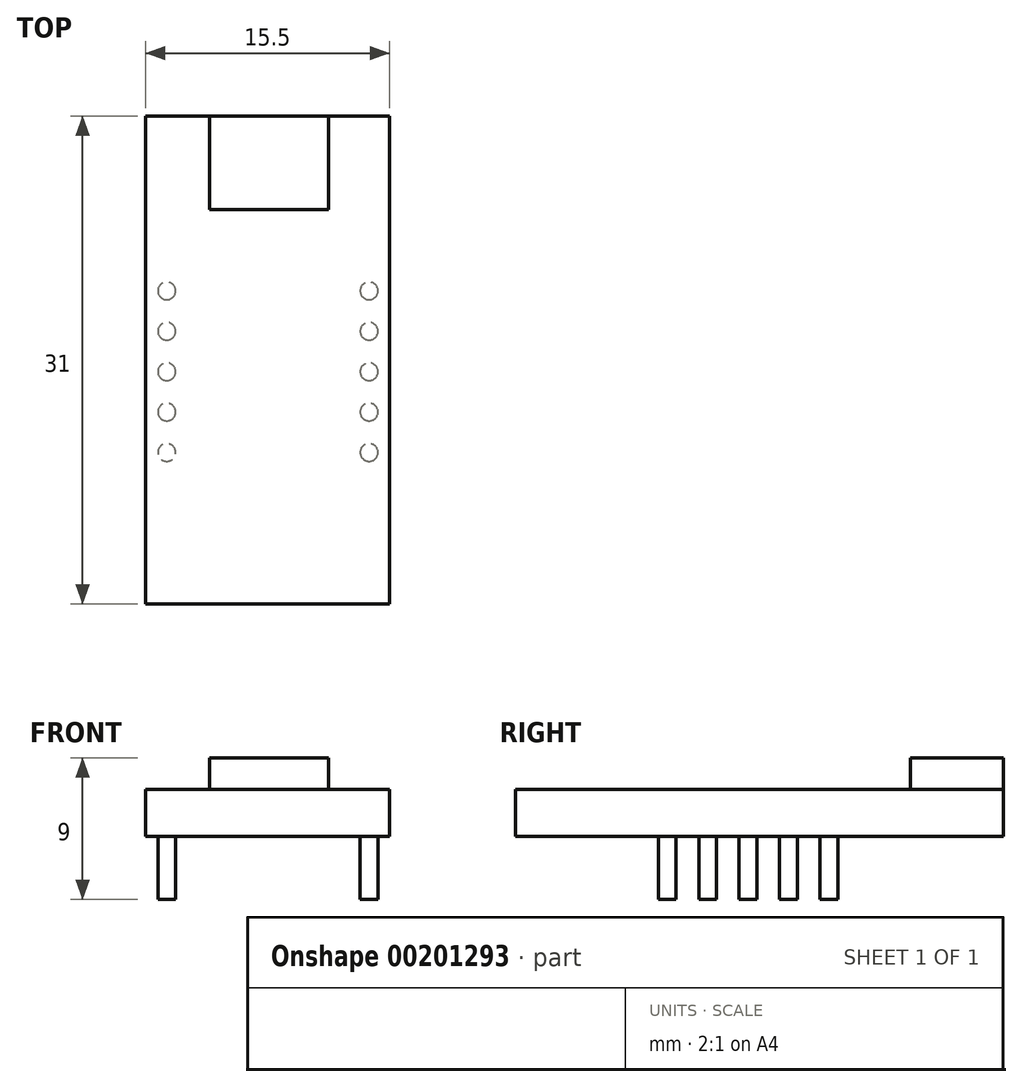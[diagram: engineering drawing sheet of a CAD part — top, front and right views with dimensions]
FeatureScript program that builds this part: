
annotation { "Feature Type Name" : "Feature", "Feature Type Description" : "" }
export const myFeature = defineFeature(function(context is Context, id is Id, definition is map)
    precondition{}
    {
        {
            var Q0;
            Q0=qCreatedBy(makeId("Top.planeOp"),FACE);
            var sketch = newSketch(context, id + "F0", { "sketchPlane" : qUnion([Q0])});
            skLineSegment(sketch, "E0.bottom", {"start": v(0, 0) * mm, "end": v(15.5, 0) * mm});
            skLineSegment(sketch, "E0.top", {"start": v(0, -31) * mm, "end": v(15.5, -31) * mm});
            skLineSegment(sketch, "E0.left", {"start": v(0, 0) * mm, "end": v(0, -31) * mm});
            skLineSegment(sketch, "E0.right", {"start": v(15.5, 0) * mm, "end": v(15.5, -31) * mm});
            skSolve(sketch);
        }
        {
            var Q0;
            Q0 = qSketchRegion(id + "F0", true);
            extrude(context, id + "F1", {"entities" : qUnion([Q0]), "depth" : 5 * mm});
        }
        {
            var Q0;
            Q0=makeQuery(id+"F1.opExtrude","CAP_FACE",FACE,{"disambiguationData":[OSD([sQuery(id+"F0.wireOp",EDGE,"E0.bottom"),sQuery(id+"F0.wireOp",EDGE,"E0.top"),sQuery(id+"F0.wireOp",EDGE,"E0.left"),sQuery(id+"F0.wireOp",EDGE,"E0.right")])],"isStart":true});
            var sketch = newSketch(context, id + "F2", { "sketchPlane" : qUnion([Q0])});
            skCircle(sketch, "E1", {"center": v(1.35, 21.36) * mm, "radius": 0.56 * mm});
            skCircle(sketch, "E2.0.1.0", {"center": v(1.35, 18.8) * mm, "radius": 0.56 * mm});
            skCircle(sketch, "E2.0.2.0", {"center": v(1.35, 16.23) * mm, "radius": 0.56 * mm});
            skCircle(sketch, "E2.0.3.0", {"center": v(1.35, 13.67) * mm, "radius": 0.56 * mm});
            skCircle(sketch, "E2.0.4.0", {"center": v(1.35, 11.1) * mm, "radius": 0.56 * mm});
            skCircle(sketch, "E2.1.0.0", {"center": v(14.2, 21.36) * mm, "radius": 0.56 * mm});
            skCircle(sketch, "E2.1.1.0", {"center": v(14.2, 18.8) * mm, "radius": 0.56 * mm});
            skCircle(sketch, "E2.1.2.0", {"center": v(14.2, 16.23) * mm, "radius": 0.56 * mm});
            skCircle(sketch, "E2.1.3.0", {"center": v(14.2, 13.67) * mm, "radius": 0.56 * mm});
            skCircle(sketch, "E2.1.4.0", {"center": v(14.2, 11.1) * mm, "radius": 0.56 * mm});
            skLineSegment(sketch, "E2.direction1", {"start": v(1.35, 21.36) * mm, "end": v(14.2, 21.36) * mm, "construction": true});
            skLineSegment(sketch, "E2.direction2", {"start": v(1.35, 21.36) * mm, "end": v(1.35, 18.8) * mm, "construction": true});
            skSolve(sketch);
        }
        {
            var Q0;
            Q0 = qSketchRegion(id + "F2", true);
            extrude(context, id + "F3", {"entities" : qUnion([Q0]), "operationType" : NewBodyOperationType.ADD, "depth" : 4 * mm});
        }
        {
            var Q0;
            Q0=makeQuery(id+"F1.opExtrude","CAP_FACE",FACE,{"disambiguationData":[OSD([sQuery(id+"F0.wireOp",EDGE,"E0.bottom"),sQuery(id+"F0.wireOp",EDGE,"E0.top"),sQuery(id+"F0.wireOp",EDGE,"E0.left"),sQuery(id+"F0.wireOp",EDGE,"E0.right")])],"isStart":false});
            var sketch = newSketch(context, id + "F4", { "sketchPlane" : qUnion([Q0])});
            skLineSegment(sketch, "E3", {"start": v(4.07, 0) * mm, "end": v(0, 0) * mm});
            skLineSegment(sketch, "E4", {"start": v(0, -31) * mm, "end": v(15.5, -31) * mm});
            skLineSegment(sketch, "E5", {"start": v(15.5, -31) * mm, "end": v(15.5, 0) * mm});
            skLineSegment(sketch, "E6", {"start": v(11.61, 0) * mm, "end": v(11.61, -5.93) * mm});
            skLineSegment(sketch, "E7", {"start": v(11.61, -5.93) * mm, "end": v(4.07, -5.93) * mm});
            skLineSegment(sketch, "E8", {"start": v(4.07, -5.93) * mm, "end": v(4.07, 0) * mm});
            skSolve(sketch);
        }
        {
            var Q0;
            Q0=makeQuery(id+"F4.imprint","IMPRINT",FACE,{"disambiguationData":[TD([[makeQuery(id+"F4.imprint","IMPRINT",EDGE,{"derivedFrom":sQuery(id+"F4.wireOp",EDGE,"E3")}),-1.0]])]});
            extrude(context, id + "F5", {"entities" : qUnion([Q0]), "operationType" : NewBodyOperationType.REMOVE, "oppositeDirection" : true, "depth" : 2 * mm});
        }
    });
